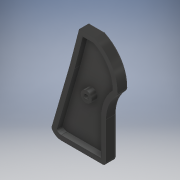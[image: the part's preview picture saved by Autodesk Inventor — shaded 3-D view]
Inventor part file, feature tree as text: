
AUTODESK INVENTOR PART (.ipt)
format: ipt  version: 2018 (Build 220112000, 112)  size: 860,160 bytes
history: native  units: in
note: dims shown in document units (in); Inventor stores cm internally (conversion verified against a paired STEP export)
features: sketch x7, extrude x6, fillet x4, projected_geometry x2, thread x1, plane x1, mirror x1, emboss x1
ambient origin geometry x8: Origin, YZ Plane, XZ Plane, XY Plane, X Axis, Y Axis, Z Axis, Center Point
bodies: Solid1 (feature_tree)
feature tree (23):
  extrude  "Extrusion1"  Depth=2.7165in
  extrude  "Extrusion2"  Depth=0.0591in TaperAngle=0.0deg
  extrude  "Extrusion7"  Depth=0.1969in
  fillet  "Fillet11"  Radius=0.1969in
  fillet  "Fillet12"  Radius=0.3543in
  fillet  "Fillet14"  Radius=0.3543in
  extrude  "Extrusion10"  Depth=0.0394in
  fillet  "Fillet15"  Radius=0.0787in
  extrude  "Extrusion15"  Depth=0.1181in
  thread  "Thread3"  [1 undecoded]
  plane  "Work Plane1"
  mirror  "Mirror1"
  extrude  "Extrusion14"  Depth=0.0394in
  emboss  "Emboss1"
  sketch  "Sketch1"  dims[d0=1.7717in d1=2.7165in]
  sketch  "Sketch2"  dims[d7=0.2756in d8=0.0in d14=0.0591in d15=0.0in]
  sketch  "Sketch8"  dims[d19=0.1181in]
  sketch  "Sketch12"  dims[d72=-0.3937in d101=7.874in d103=0.3937in d105=7.874in d107=0.3937in d109=7.874in d111=0.3937in d113=7.874in d115=0.3937in d117=7.874in d119=0.3937in d121=7.874in d123=0.3937in d125=7.874in d127=0.3937in d129=7.874in d131=0.3937in d173=0.1969in d174=0.1969in d175=0.3543in d176=0.3543in]
  projected_geometry  "Projected Loop5"
  sketch  "Sketch13"  dims[d177=0.0315in d178=0.0in d185=0.0394in d186=0.0787in]
  sketch  "Sketch14"  dims[d191=0.0787in d195=0.1181in d196=0.0787in]
  projected_geometry  "Projected Loop8"
  sketch  "Sketch16"  dims[d197=0.1565in d198=0.0in d199=0.0394in d846=0.0472in d847=0.0in d903=0.0394in d904=0.0394in d905=0.0394in d906=0.0394in d907=0.0394in d908=0.0394in d909=0.0394in d910=0.0394in d911=0.0394in d912=0.0394in d913=0.0394in d914=0.0394in d915=0.0394in d916=0.0394in d932=0.0394in d933=0.0394in d934=0.0394in d935=0.0394in d936=0.0394in d937=0.0394in d938=0.0394in d939=0.0394in d940=0.0394in d941=0.0394in d942=0.0394in d943=0.0394in d944=0.0394in d945=0.0394in d946=0.0394in d948=0.0394in d954=0.0394in d958=0.0394in d959=0.0394in d960=0.0039in d961=0.0in d962=0.3937in d963=0.0in d964=0.0039in d965=0.0in]
note: 1 required parameter value undecoded (feature->parameter linkage not recoverable at this tier; creation-order binding heuristic only, values carry confidence <= 0.55)
